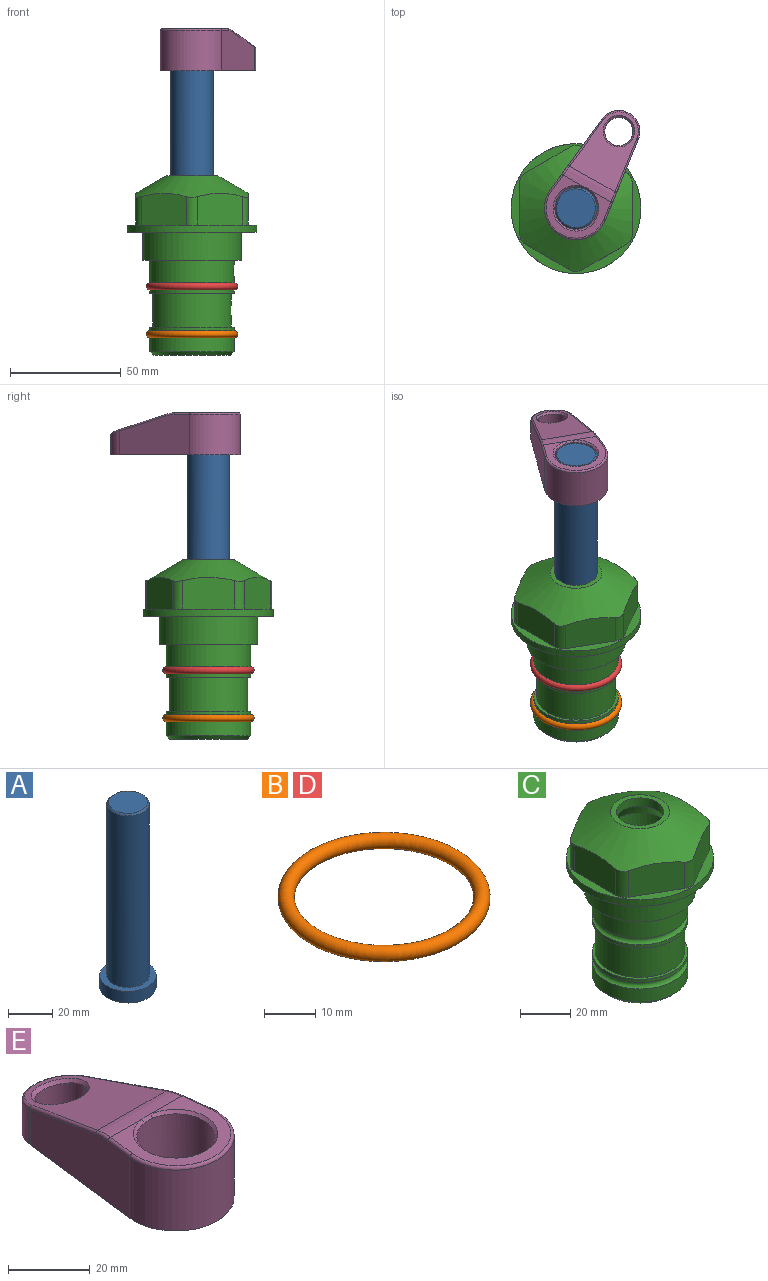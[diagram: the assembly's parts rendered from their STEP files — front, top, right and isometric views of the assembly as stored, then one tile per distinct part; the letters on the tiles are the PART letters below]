
ASSEMBLY  parts=5 mates=4
PART A: 6 faces, bbox 25.4x25.4x101.6 mm
  f0: plane 17.46x17.46mm, normal (0,0,1), area 239.5mm2, adj f5
  f1: plane 25.4x25.4mm, normal (0,0,-1), area 506.7mm2, adj f2
  f2: cylinder r=12.7mm len=25.4mm, axis (0,0,1), area 506.7mm2, adj f1,f3
  f3: plane 25.4x25.4mm, normal (0,0,1), area 221.7mm2, adj f2,f4
  f4: cylinder r=9.53mm len=94.46mm, axis (0,0,1), area 5653mm2, adj f3,f5
  f5: cone r=8.73mm half-angle=45deg, axis (0,0,-1), area 64.4mm2, adj f0,f4
PART B: 1 faces, bbox 44.7x44.7x3.2 mm
  f0: torus R=19.05mm, axis (0,0,1), area 1193.9mm2
PART C: 36 faces, bbox 58.7x58.7x81 mm
  f0: cylinder r=17.78mm len=35.56mm, axis (0,0,1), area 1670.8mm2, adj f23,f24,f31
  f1: cylinder r=19.05mm len=38.1mm, axis (0,0,1), area 1191.9mm2, adj f26,f27,f30
  f2: plane 58.66x58.66mm, normal (0,0,-1), area 1150.6mm2, adj f3,f28
  f3: cylinder r=29.33mm len=58.66mm, axis (0,0,-1), area 585.1mm2, adj f2,f4
  f4: plane 58.66x58.66mm, normal (0,0,1), area 475.9mm2, adj f3,f5,f6,f7,f8,f9,f10,f11
  f5: plane 20.32x14.34mm, normal (-0.5,0.87,0), area 324.4mm2, adj f4,f15,f16,f17
  f6: plane 20.32x14.34mm, normal (0.5,0.87,0), area 324.4mm2, adj f4,f14,f15,f17
  f7: plane 23.48x14.34mm, normal (1,0,0), area 324.4mm2, adj f4,f13,f14,f17
  f8: plane 20.32x14.34mm, normal (0.5,-0.87,0), area 324.4mm2, adj f4,f12,f13,f17
  f9: plane 20.32x14.34mm, normal (-0.5,-0.87,0), area 324.4mm2, adj f4,f11,f12,f17
  f10: plane 23.48x14.34mm, normal (-1,0,0), area 324.4mm2, adj f4,f11,f16,f17
  f11: cylinder r=5.08mm len=12.85mm, axis (0,0,-1), area 67.2mm2, adj f4,f9,f10,f17
  f12: cylinder r=5.08mm len=12.85mm, axis (0,0,-1), area 67.2mm2, adj f4,f8,f9,f17
  f13: cylinder r=5.08mm len=12.85mm, axis (0,0,-1), area 67.2mm2, adj f4,f7,f8,f17
  f14: cylinder r=5.08mm len=12.85mm, axis (0,0,-1), area 67.2mm2, adj f4,f6,f7,f17
  f15: cylinder r=5.08mm len=12.85mm, axis (0,0,-1), area 67.2mm2, adj f4,f5,f6,f17
  f16: cylinder r=5.08mm len=12.85mm, axis (0,0,-1), area 67.2mm2, adj f4,f5,f10,f17
  f17: cone r=11.73mm half-angle=60deg, axis (0,0,-1), area 2071.8mm2, adj f5,f6,f7,f8,f9,f10,f11,f12
  f18: plane 23.46x23.46mm, normal (0,0,1), area 147.4mm2, adj f17,f35
  f19: plane 34.93x34.93mm, normal (0,0,-1), area 958mm2, adj f29
  f20: cylinder r=19.05mm len=38.1mm, axis (0,0,1), area 760.1mm2, adj f21,f29
  f21: torus R=19.05mm, axis (0,0,1), area 565.3mm2, adj f20,f22
  f22: cylinder r=19.05mm len=38.1mm, axis (0,0,1), area 190mm2, adj f21,f23
  f23: plane 38.1x38.1mm, normal (0,0,1), area 146.9mm2, adj f0,f22
  f24: plane 38.1x38.1mm, normal (0,0,-1), area 146.9mm2, adj f0,f25
  f25: cylinder r=19.05mm len=38.1mm, axis (0,0,1), area 190mm2, adj f24,f26
  f26: torus R=19.05mm, axis (0,0,1), area 565.3mm2, adj f1,f25
  f27: plane 44.45x44.45mm, normal (0,0,-1), area 411.7mm2, adj f1,f28
  f28: cylinder r=22.23mm len=44.45mm, axis (0,0,1), area 1773.5mm2, adj f2,f27
  f29: cone r=19.05mm half-angle=45deg, axis (0,0,1), area 257.5mm2, adj f19,f20
  f30: cylinder r=3.17mm len=6.75mm, axis (-1,0,0), area 128mm2, adj f1,f33
  f31: cylinder r=3.17mm len=6.35mm, axis (-1,0,0), area 102.5mm2, adj f0,f33
  f32: plane 25.4x25.4mm, normal (0,0,1), area 506.7mm2, adj f33
  f33: cylinder r=12.7mm len=66.42mm, axis (0,0,-1), area 5236.2mm2, adj f30,f31,f32,f34
  f34: cone r=9.53mm half-angle=30deg, axis (0,0,-1), area 443.4mm2, adj f33,f35
  f35: cylinder r=9.53mm len=19.05mm, axis (0,0,-1), area 240.9mm2, adj f18,f34
PART D: same geometry as B
PART E: 31 faces, bbox 31.7x65.5x19.8 mm
  f0: plane 39.12x18.26mm, normal (0.99,0.12,0), area 612.2mm2, adj f1,f4,f7,f11,f13,f15
  f1: cylinder r=9.53mm len=18.91mm, axis (0,0,-1), area 296.1mm2, adj f0,f2,f7,f17
  f2: plane 39.12x18.26mm, normal (-0.99,0.12,0), area 612.2mm2, adj f1,f4,f7,f12,f14,f16
  f3: cylinder r=6.35mm len=12.7mm, axis (0,0,-1), area 362.4mm2, adj f7,f18
  f4: cylinder r=14.29mm len=28.58mm, axis (0,0,-1), area 882.2mm2, adj f0,f2,f7,f10
  f5: cylinder r=9.53mm len=19.05mm, axis (0,0,-1), area 1092.6mm2, adj f7,f19,f20
  f6: plane 26.99x23.69mm, normal (0,0,1), area 216.2mm2, adj f9,f10,f11,f12,f19
  f7: plane 63.5x28.58mm, normal (0,0,-1), area 661.8mm2, adj f0,f1,f2,f3,f4,f5,f22,f23
  f8: plane 33.52x23.6mm, normal (0,0.26,0.97), area 486mm2, adj f9,f15,f16,f17,f18
  f9: cylinder r=19.05mm len=24.72mm, axis (1,0,0), area 120.4mm2, adj f6,f8,f13,f14,f20
  f10: torus R=13.49mm, axis (0,0,1), area 59mm2, adj f4,f6,f11,f12
  f11: cylinder r=0.79mm len=8.67mm, axis (0.12,-0.99,0), area 10.8mm2, adj f0,f6,f10,f13
  f12: cylinder r=0.79mm len=8.67mm, axis (0.12,0.99,0), area 10.8mm2, adj f2,f6,f10,f14
  f13: bspline ~4.95x1.42mm, area 6.1mm2, adj f0,f9,f11,f15
  f14: bspline ~4.95x1.42mm, area 6.1mm2, adj f2,f9,f12,f16
  f15: cylinder r=0.79mm len=25.95mm, axis (0.12,-0.96,0.26), area 32.9mm2, adj f0,f8,f13,f17
  f16: cylinder r=0.79mm len=25.95mm, axis (0.12,0.96,-0.26), area 32.9mm2, adj f2,f8,f14,f17
  f17: bspline ~18.91x8.38mm, area 30mm2, adj f1,f8,f15,f16
  f18: bspline ~14.29x14.29mm, area 48.3mm2, adj f3,f8
  f19: cone r=9.53mm half-angle=45deg, axis (0,0,1), area 66.5mm2, adj f5,f6,f20
  f20: bspline ~3.22x0.96mm, area 3.5mm2, adj f5,f9,f19
  f21: plane 2.75x2.72mm, normal (0,0,-1), area 2.9mm2, adj f23,f25,f28
  f22: plane 23.05x15.88mm, normal (-0.99,-0.12,0), area 323.6mm2, adj f7,f25,f26,f27,f28,f29
  f23: plane 23.05x15.88mm, normal (0.99,-0.12,0), area 323.6mm2, adj f7,f21,f25,f27,f28,f30
  f24: cylinder r=9.53mm len=10.69mm, axis (0,0,-1), area 114.7mm2, adj f7,f27,f29,f30
  f25: cylinder r=12.7mm len=20.59mm, axis (0,0,-1), area 381.1mm2, adj f7,f21,f22,f23,f26,f28
  f26: plane 2.75x2.72mm, normal (0,0,-1), area 2.9mm2, adj f22,f25,f28
  f27: plane 19.72x18.37mm, normal (0,-0.26,-0.97), area 291.8mm2, adj f22,f23,f24,f28,f29,f30
  f28: cylinder r=15.88mm len=19.92mm, axis (1,0,0), area 54.8mm2, adj f21,f22,f23,f25,f26,f27
  f29: cylinder r=1.59mm len=11mm, axis (0,0,-1), area 34.7mm2, adj f7,f22,f24,f27
  f30: cylinder r=1.59mm len=11mm, axis (0,0,-1), area 34.7mm2, adj f7,f23,f24,f27
PLACE A rot(axis=(0,0,-1),29.2deg) t=(0,0,27.55)mm
PLACE B t=(0,0,-21.59)mm
PLACE C at identity fixed
PLACE D at identity
PLACE E rot(axis=(0,0,-1),29.2deg) t=(0,0,28.35)mm
MATE fastened D.f0 <-> C.f0  axis (0,0,1) through (0,0,-24.51)mm
MATE fastened B.f0 <-> C.f0  axis (0,0,1) through (0,0,-46.1)mm
MATE fastened E.f4 <-> A.f2  axis (0,0,-1) through (0,0,91.05)mm
MATE cylindrical A.f2 <-> C.f0  axis (0,0,1) through (0,0,-10.55)mm
